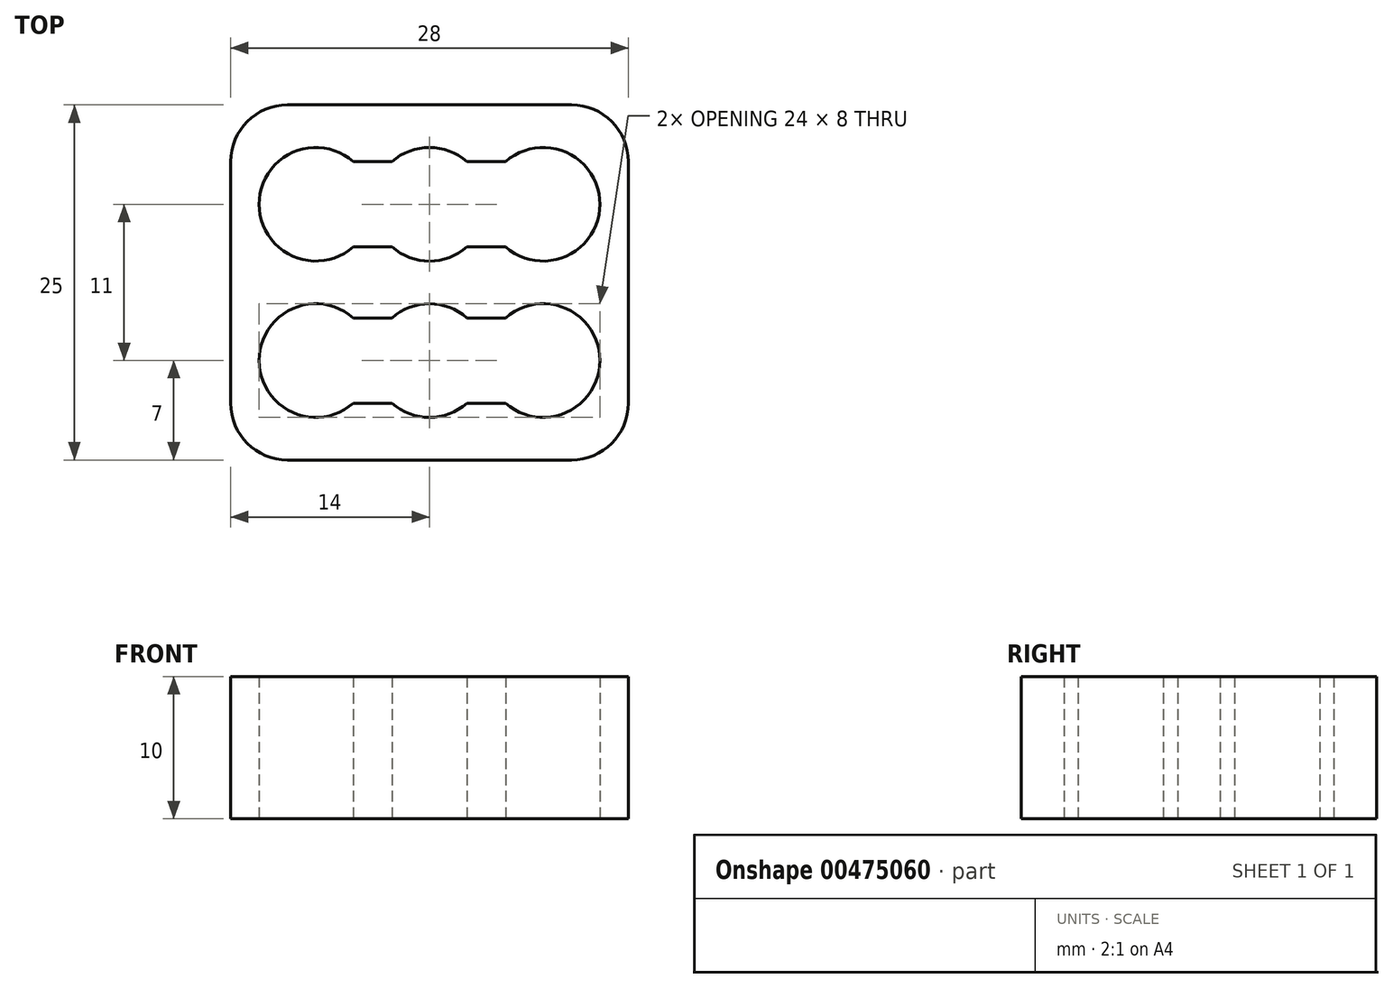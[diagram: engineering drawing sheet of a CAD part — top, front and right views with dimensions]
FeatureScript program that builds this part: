
annotation { "Feature Type Name" : "Feature", "Feature Type Description" : "" }
export const myFeature = defineFeature(function(context is Context, id is Id, definition is map)
    precondition{}
    {
        {
            var Q0;
            Q0=qCreatedBy(makeId("Top.planeOp"),FACE);
            var sketch = newSketch(context, id + "F0", { "sketchPlane" : qUnion([Q0])});
            skArc(sketch, "E0", {"start": v(-2.65, -8.6) * mm, "mid": v(0, -9.6) * mm, "end": v(2.65, -8.6) * mm});
            skArc(sketch, "E1", {"start": v(5.35, -8.6) * mm, "mid": v(8, -9.6) * mm, "end": v(10.65, -8.6) * mm});
            skArc(sketch, "E2", {"start": v(-5.35, -2.6) * mm, "mid": v(-8, -1.6) * mm, "end": v(-10.65, -2.6) * mm});
            skLineSegment(sketch, "E3", {"start": v(-18.64, -0.1) * mm, "end": v(35.35, -0.1) * mm, "construction": true});
            skArc(sketch, "E4.MirrorC", {"start": v(-5.35, 2.4) * mm, "mid": v(-12, 5.4) * mm, "end": v(-5.35, 8.4) * mm});
            skArc(sketch, "E5.MirrorC", {"start": v(2.65, 2.4) * mm, "mid": v(0, 1.4) * mm, "end": v(-2.65, 2.4) * mm});
            skArc(sketch, "E6.MirrorC", {"start": v(10.65, 2.4) * mm, "mid": v(8, 1.4) * mm, "end": v(5.35, 2.4) * mm});
            skLineSegment(sketch, "E7", {"start": v(14, -12.6) * mm, "end": v(-11.26, -12.6) * mm});
            skLineSegment(sketch, "E8", {"start": v(14, 12.4) * mm, "end": v(-14, 12.4) * mm});
            skLineSegment(sketch, "E9", {"start": v(-14, 12.4) * mm, "end": v(-14, 5.4) * mm});
            skLineSegment(sketch, "E10", {"start": v(-11.26, -12.6) * mm, "end": v(-14, -12.6) * mm});
            skLineSegment(sketch, "E11.trimOffspring", {"start": v(-2.65, 8.4) * mm, "end": v(-5.35, 8.4) * mm});
            skLineSegment(sketch, "E12.trimOffspring", {"start": v(5.35, 8.4) * mm, "end": v(2.65, 8.4) * mm});
            skArc(sketch, "E13.trimOffspring", {"start": v(5.35, 8.4) * mm, "mid": v(8, 9.4) * mm, "end": v(10.65, 8.4) * mm});
            skArc(sketch, "E14.trimOffspring", {"start": v(-2.65, 8.4) * mm, "mid": v(0, 9.4) * mm, "end": v(2.65, 8.4) * mm});
            skLineSegment(sketch, "E15", {"start": v(-5.35, -2.6) * mm, "end": v(-2.65, -2.6) * mm});
            skLineSegment(sketch, "E16", {"start": v(-5.35, -8.6) * mm, "end": v(-2.65, -8.6) * mm});
            skLineSegment(sketch, "E17.trimOffspring", {"start": v(2.65, -2.6) * mm, "end": v(5.35, -2.6) * mm});
            skLineSegment(sketch, "E18.trimOffspring", {"start": v(2.65, -8.6) * mm, "end": v(5.35, -8.6) * mm});
            skArc(sketch, "E19.trimOffspring", {"start": v(2.65, -2.6) * mm, "mid": v(0, -1.6) * mm, "end": v(-2.65, -2.6) * mm});
            skArc(sketch, "E20.trimOffspring", {"start": v(10.65, -2.6) * mm, "mid": v(8, -1.6) * mm, "end": v(5.35, -2.6) * mm});
            skArc(sketch, "E21.trimOffspring", {"start": v(-10.65, -8.6) * mm, "mid": v(-8, -9.6) * mm, "end": v(-5.35, -8.6) * mm});
            skLineSegment(sketch, "E22.trimOffspring", {"start": v(-2.65, 2.4) * mm, "end": v(-5.35, 2.4) * mm});
            skLineSegment(sketch, "E23.trimOffspring", {"start": v(5.35, 2.4) * mm, "end": v(2.65, 2.4) * mm});
            skLineSegment(sketch, "E24", {"start": v(14, 8.4) * mm, "end": v(14, 12.4) * mm});
            skLineSegment(sketch, "E25", {"start": v(14, 2.4) * mm, "end": v(14, -12.6) * mm});
            skPoint(sketch, "E26.end.orphan", {"position": v(18.26, 18) * mm});
            skPoint(sketch, "E27.end.orphan", {"position": v(22, 14) * mm});
            skPoint(sketch, "E27.start.orphan", {"position": v(22, 18) * mm});
            skPoint(sketch, "E28.center.orphan", {"position": v(16, -5.6) * mm});
            skPoint(sketch, "E29.start.orphan", {"position": v(22, 8) * mm});
            skArc(sketch, "E30", {"start": v(10.65, -8.6) * mm, "mid": v(12, -5.6) * mm, "end": v(10.65, -2.6) * mm});
            skPoint(sketch, "E31.end.orphan", {"position": v(14, -5.1) * mm});
            skPoint(sketch, "E31.start.orphan", {"position": v(12, -5.6) * mm});
            skLineSegment(sketch, "E32", {"start": v(-19.3, 5.4) * mm, "end": v(25.98, 5.4) * mm, "construction": true});
            skLineSegment(sketch, "E33", {"start": v(22.82, -5.6) * mm, "end": v(-23.22, -5.6) * mm, "construction": true});
            skArc(sketch, "E34", {"start": v(-10.65, -2.6) * mm, "mid": v(-12, -5.6) * mm, "end": v(-10.65, -8.6) * mm});
            skPoint(sketch, "E35.start.orphan", {"position": v(-14, -8.6) * mm});
            skPoint(sketch, "E36.trimOffspring.end.orphan", {"position": v(-14, -2.6) * mm});
            skLineSegment(sketch, "E37", {"start": v(-14, -12.6) * mm, "end": v(-14, 5.4) * mm});
            skLineSegment(sketch, "E38", {"start": v(14, 2.4) * mm, "end": v(14, 8.4) * mm});
            skArc(sketch, "E39", {"start": v(10.65, 2.4) * mm, "mid": v(12, 5.4) * mm, "end": v(10.65, 8.4) * mm});
            skSolve(sketch);
        }
        {
            var Q0;
            Q0=makeQuery(id+"F0.imprint","IMPRINT",FACE,{"disambiguationData":[TD([[makeQuery(id+"F0.imprint","IMPRINT",EDGE,{"derivedFrom":sQuery(id+"F0.wireOp",EDGE,"E0")}),-1.0]])]});
            extrude(context, id + "F1", {"entities" : qUnion([Q0]), "flatOperationType" : FlatOperationType.REMOVE, "offsetDistance" : 25 * mm, "depth" : 10 * mm, "domain" : OperationDomain.MODEL});
        }
        {
            var Q0;
            Q0=makeQuery(id+"F1.opExtrude","SWEPT_EDGE",EDGE,{"disambiguationData":[OSD([sQuery(id+"F0.wireOp",EDGE,"E8"),sQuery(id+"F0.wireOp",EDGE,"E9")])]});
            var Q1;
            Q1=makeQuery(id+"F1.opExtrude","SWEPT_EDGE",EDGE,{"disambiguationData":[OSD([sQuery(id+"F0.wireOp",EDGE,"E7"),sQuery(id+"F0.wireOp",EDGE,"E25")])]});
            var Q2;
            Q2=makeQuery(id+"F1.opExtrude","SWEPT_EDGE",EDGE,{"disambiguationData":[OSD([sQuery(id+"F0.wireOp",EDGE,"ayJ3G5tn-fuyW-xk8k-UtQO-Z51El7EXuUbb"),sQuery(id+"F0.wireOp",EDGE,"E10")])]});
            var Q3;
            Q3=makeQuery(id+"F1.opExtrude","SWEPT_EDGE",EDGE,{"disambiguationData":[OSD([sQuery(id+"F0.wireOp",EDGE,"E8"),sQuery(id+"F0.wireOp",EDGE,"E24")])]});
            fillet(context, id + "F2", {"entities" : qUnion([Q0, Q1, Q2, Q3]), "radius" : 4 * mm, "tangentPropagation" : true, "allowEdgeOverflow" : false});
        }
    });
